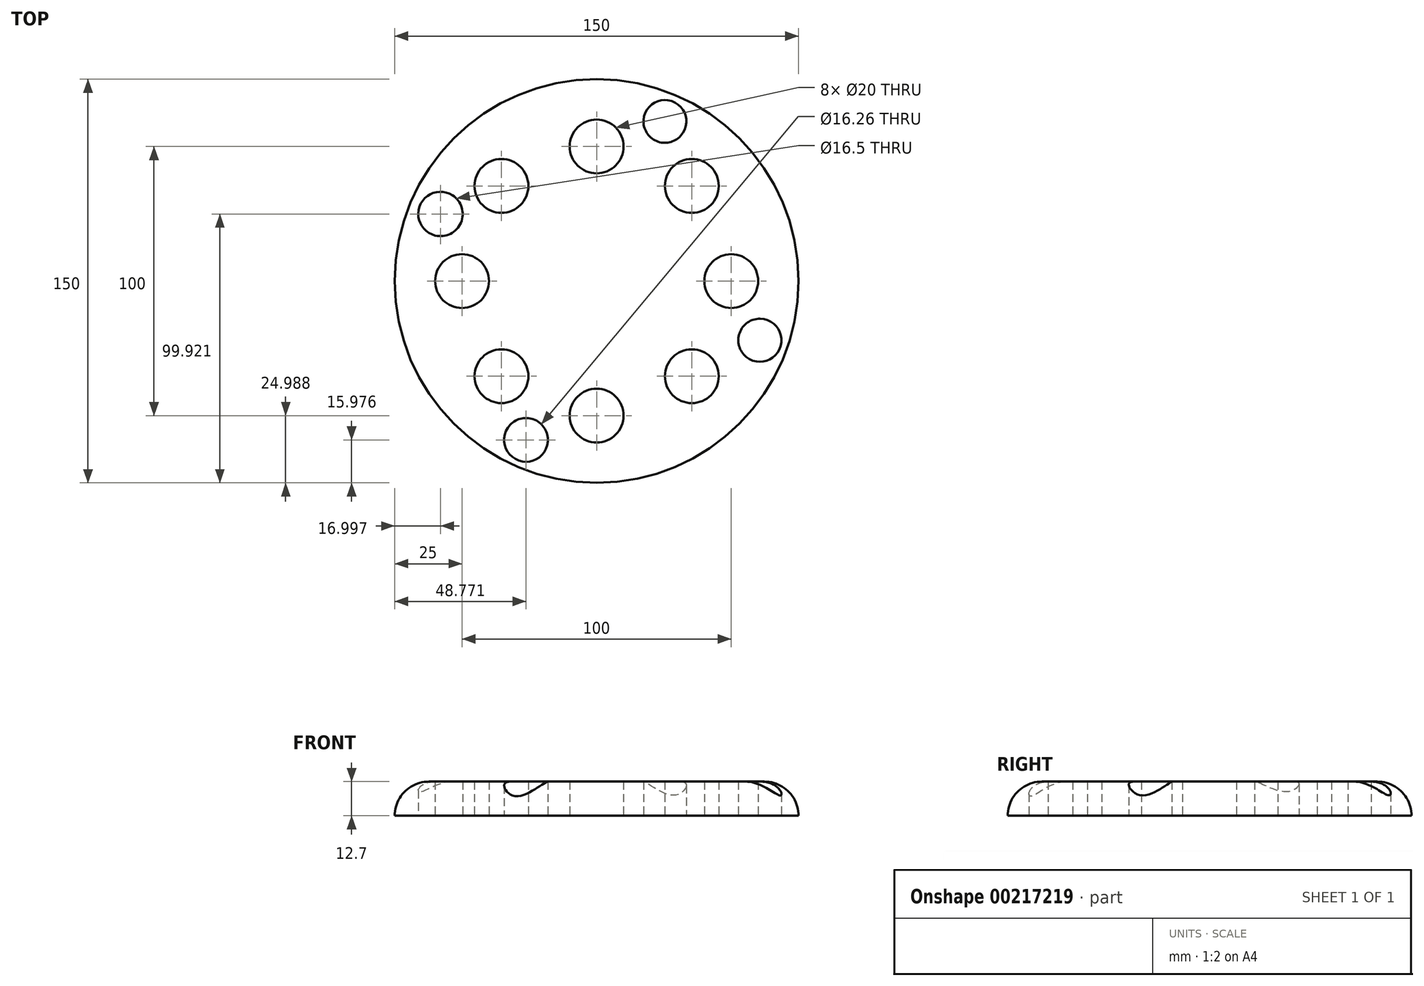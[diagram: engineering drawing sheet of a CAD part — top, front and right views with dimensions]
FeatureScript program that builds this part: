
annotation { "Feature Type Name" : "Feature", "Feature Type Description" : "" }
export const myFeature = defineFeature(function(context is Context, id is Id, definition is map)
    precondition{}
    {
        {
            var Q0;
            Q0=qCreatedBy(makeId("Top.planeOp"),FACE);
            var sketch = newSketch(context, id + "F0", { "sketchPlane" : qUnion([Q0])});
            skCircle(sketch, "E0", {"center": v(0, 0) * mm, "radius": 75 * mm});
            skCircle(sketch, "E1", {"center": v(0, 49.99) * mm, "radius": 10 * mm});
            skCircle(sketch, "E2.1.0", {"center": v(-35.36, 35.34) * mm, "radius": 10 * mm});
            skCircle(sketch, "E2.2.0", {"center": v(-50, -0.01) * mm, "radius": 10 * mm});
            skCircle(sketch, "E2.3.0", {"center": v(-35.36, -35.37) * mm, "radius": 10 * mm});
            skCircle(sketch, "E2.4.0", {"center": v(0, -50.01) * mm, "radius": 10 * mm});
            skCircle(sketch, "E2.5.0", {"center": v(35.36, -35.37) * mm, "radius": 10 * mm});
            skCircle(sketch, "E2.6.0", {"center": v(50, -0.01) * mm, "radius": 10 * mm});
            skCircle(sketch, "E2.7.0", {"center": v(35.36, 35.34) * mm, "radius": 10 * mm});
            skPoint(sketch, "E2.center", {"position": v(0, -0.01) * mm});
            skCircle(sketch, "E3", {"center": v(25.36, 59.32) * mm, "radius": 7.96 * mm});
            skCircle(sketch, "E4", {"center": v(-26.23, -59.02) * mm, "radius": 8.13 * mm});
            skCircle(sketch, "E5", {"center": v(-58, 24.92) * mm, "radius": 8.25 * mm});
            skCircle(sketch, "E6", {"center": v(60.64, -22) * mm, "radius": 8 * mm});
            skSolve(sketch);
        }
        {
            var Q0;
            Q0 = qSketchRegion(id + "F0", true);
            extrude(context, id + "F1", {"entities" : qUnion([Q0]), "depth" : 12.7 * mm});
        }
        {
            var Q0;
            Q0=makeQuery(id+"F1.opExtrude","CAP_EDGE",EDGE,{"disambiguationData":[OSD([sQuery(id+"F0.wireOp",EDGE,"E0")])],"isStart":false});
            fillet(context, id + "F2", {"entities" : qUnion([Q0]), "radius" : 12.7 * mm, "tangentPropagation" : true, "allowEdgeOverflow" : false});
        }
        {
            var Q0;
            Q0=sQuery(id+"F0.wireOp",EDGE,"E5");
            var Q1;
            Q1=sQuery(id+"F0.wireOp",EDGE,"E4");
            var Q2;
            Q2=sQuery(id+"F0.wireOp",EDGE,"E6");
            var Q3;
            Q3=sQuery(id+"F0.wireOp",EDGE,"E3");
            var Q4;
            Q4=sQuery(id+"F0.wireOp",EDGE,"E2.5.0");
            extrude(context, id + "F3", {"bodyType" : ToolBodyType.SURFACE, "surfaceEntities" : qUnion([Q0, Q1, Q2, Q3, Q4]), "oppositeDirection" : true, "depth" : 100 * mm});
        }
    });
